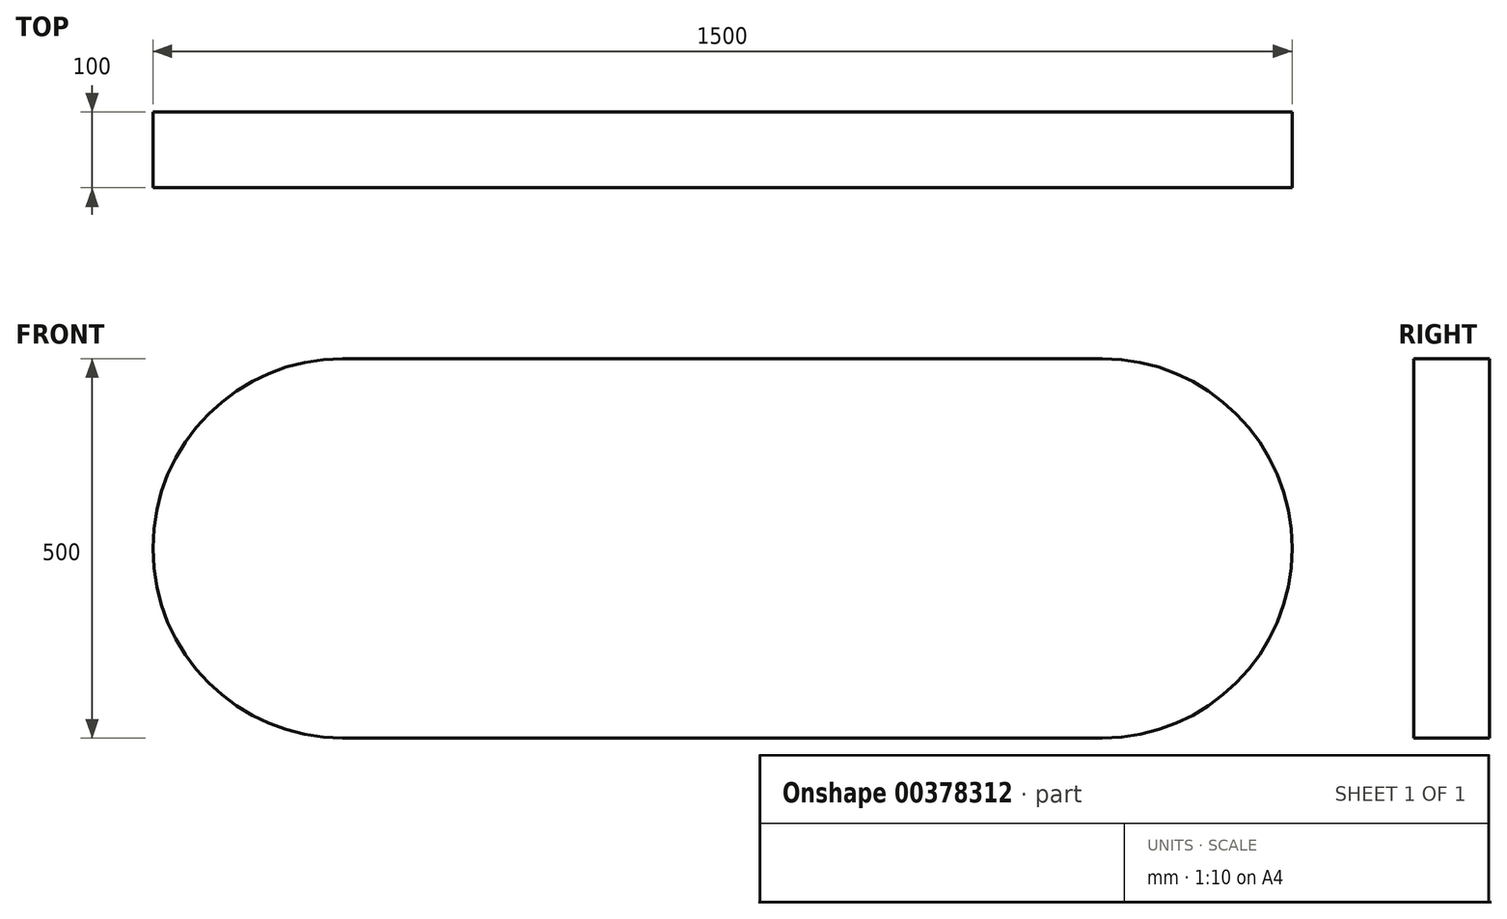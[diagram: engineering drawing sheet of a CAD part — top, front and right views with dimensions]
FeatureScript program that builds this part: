
annotation { "Feature Type Name" : "Feature", "Feature Type Description" : "" }
export const myFeature = defineFeature(function(context is Context, id is Id, definition is map)
    precondition{}
    {
        {
            var Q0;
            Q0=qCreatedBy(makeId("Front.planeOp"),FACE);
            var sketch = newSketch(context, id + "F0", { "sketchPlane" : qUnion([Q0])});
            skLineSegment(sketch, "E0", {"start": v(500, 0) * mm, "end": v(-500, 0) * mm});
            skArc(sketch, "E1", {"start": v(-500, 250) * mm, "mid": v(-750, 0) * mm, "end": v(-500, -250) * mm});
            skArc(sketch, "E2", {"start": v(500, -250) * mm, "mid": v(750, 0) * mm, "end": v(500, 250) * mm});
            skLineSegment(sketch, "E3", {"start": v(-500, 250) * mm, "end": v(500, 250) * mm});
            skLineSegment(sketch, "E4", {"start": v(500, -250) * mm, "end": v(-500, -250) * mm});
            skLineSegment(sketch, "E5", {"start": v(-255.05, -50) * mm, "end": v(255.05, -50) * mm});
            skLineSegment(sketch, "E6", {"start": v(-300, -150) * mm, "end": v(300, -150) * mm});
            skSolve(sketch);
        }
        {
            var Q0;
            Q0 = qSketchRegion(id + "F0", true);
            extrude(context, id + "F1", {"entities" : qUnion([Q0]), "oppositeDirection" : true, "depth" : 100 * mm});
        }
    });
